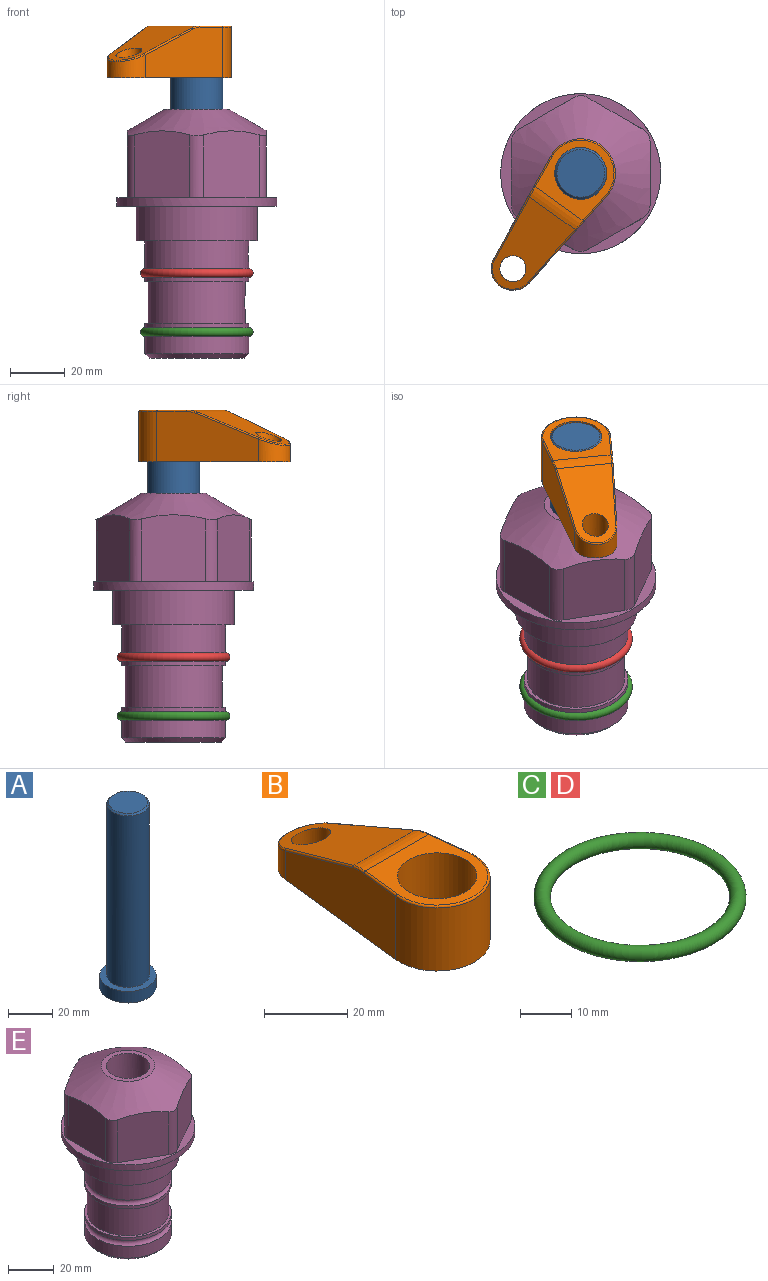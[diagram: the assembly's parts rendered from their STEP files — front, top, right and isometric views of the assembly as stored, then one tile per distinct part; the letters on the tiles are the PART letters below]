
ASSEMBLY  parts=5 mates=3
PART A: 6 faces, bbox 25.4x25.4x101.6 mm
  f0: plane 17.46x17.46mm, normal (0,0,1), area 239.5mm2, adj f5
  f1: plane 25.4x25.4mm, normal (0,0,-1), area 506.7mm2, adj f2
  f2: cylinder r=12.7mm len=25.4mm, axis (0,0,1), area 506.7mm2, adj f1,f3
  f3: plane 25.4x25.4mm, normal (0,0,1), area 221.7mm2, adj f2,f4
  f4: cylinder r=9.53mm len=94.46mm, axis (0,0,1), area 5653mm2, adj f3,f5
  f5: cone r=8.73mm half-angle=45deg, axis (0,0,-1), area 64.4mm2, adj f0,f4
PART B: 44 faces, bbox 27.5x64.5x19.1 mm
  f0: plane 2.3x0.95mm, normal (0,0,-1), area 1mm2, adj f25,f30,f34
  f1: plane 63.5x25.4mm, normal (0,0,-1), area 561.7mm2, adj f2,f3,f4,f5,f6,f7,f19,f20
  f2: cylinder r=12.7mm len=25.4mm, axis (0,0,-1), area 792.2mm2, adj f1,f3,f5,f13
  f3: plane 42.33x18.54mm, normal (0.99,0.11,0), area 647mm2, adj f1,f2,f4,f11,f12,f14
  f4: cylinder r=7.94mm len=15.78mm, axis (0,0,-1), area 158.6mm2, adj f1,f3,f5,f16
  f5: plane 42.33x18.54mm, normal (-0.99,0.11,0), area 647mm2, adj f1,f2,f4,f15,f17,f18
  f6: cylinder r=9.53mm len=19.05mm, axis (0,0,-1), area 1140.1mm2, adj f1,f8
  f7: cylinder r=4.76mm len=10.98mm, axis (0,0,-1), area 276.1mm2, adj f1,f9
  f8: plane 25.83x24.38mm, normal (0,0,1), area 262.2mm2, adj f6,f10,f11,f13,f15
  f9: plane 32.49x20.55mm, normal (0,0.34,0.94), area 489.9mm2, adj f7,f10,f14,f16,f18
  f10: cylinder r=12.7mm len=21.49mm, axis (-1,0,0), area 93.2mm2, adj f8,f9,f12,f17
  f11: cylinder r=0.51mm len=12.34mm, axis (0.11,-0.99,0), area 9.9mm2, adj f3,f8,f12,f13
  f12: bspline ~7.62x1.64mm, area 3.5mm2, adj f3,f10,f11,f14
  f13: torus R=12.19mm, axis (0,0,1), area 33.6mm2, adj f2,f8,f11,f15
  f14: cylinder r=0.51mm len=26.01mm, axis (0.1,-0.93,0.34), area 21.6mm2, adj f3,f9,f12,f16
  f15: cylinder r=0.51mm len=12.34mm, axis (0.11,0.99,0), area 9.9mm2, adj f5,f8,f13,f17
  f16: bspline ~15.78x7.05mm, area 15.7mm2, adj f4,f9,f14,f18
  f17: bspline ~7.62x1.64mm, area 3.5mm2, adj f5,f10,f15,f18
  f18: cylinder r=0.51mm len=26.01mm, axis (0.1,0.93,-0.34), area 21.6mm2, adj f5,f9,f16,f17
  f19: plane 21.6x14.29mm, normal (-0.99,-0.11,0), area 242.6mm2, adj f1,f26,f28,f34,f36,f38
  f20: plane 21.6x14.29mm, normal (0.99,-0.11,0), area 242.6mm2, adj f1,f27,f29,f37,f39,f41
  f21: cylinder r=12.7mm len=14.29mm, axis (0,0,-1), area 173.2mm2, adj f1,f26,f27,f30,f31,f33
  f22: cylinder r=7.94mm len=7.63mm, axis (0,0,-1), area 53.8mm2, adj f1,f28,f29,f42
  f23: plane 2.3x0.95mm, normal (0,0,-1), area 1mm2, adj f25,f33,f37
  f24: plane 17.94x12.32mm, normal (0,-0.34,-0.94), area 191.2mm2, adj f25,f38,f41,f42
  f25: cylinder r=9.53mm len=12.93mm, axis (-1,0,0), area 37.5mm2, adj f0,f23,f24,f31,f36,f39
  f26: cylinder r=1.59mm len=14.29mm, axis (0,0,-1), area 49mm2, adj f1,f19,f21,f32
  f27: cylinder r=1.59mm len=14.29mm, axis (0,0,-1), area 49mm2, adj f1,f20,f21,f35
  f28: cylinder r=1.59mm len=7.28mm, axis (0,0,-1), area 22.1mm2, adj f1,f19,f22,f40
  f29: cylinder r=1.59mm len=7.28mm, axis (0,0,-1), area 22.1mm2, adj f1,f20,f22,f43
  f30: torus R=14.29mm, axis (0,0,1), area 5.8mm2, adj f0,f21,f31,f32
  f31: bspline ~11.06x2.73mm, area 20.8mm2, adj f21,f25,f30,f33
  f32: sphere r=1.59mm, area 5.4mm2, adj f26,f30,f34
  f33: torus R=14.29mm, axis (0,0,1), area 5.8mm2, adj f21,f23,f31,f35
  f34: cylinder r=1.59mm len=1.68mm, axis (-0.11,0.99,0), area 2.4mm2, adj f0,f19,f32,f36
  f35: sphere r=1.59mm, area 5.4mm2, adj f27,f33,f37
  f36: bspline ~5.82x2.33mm, area 7.7mm2, adj f19,f25,f34,f38
  f37: cylinder r=1.59mm len=1.68mm, axis (0.11,0.99,0), area 2.4mm2, adj f20,f23,f35,f39
  f38: cylinder r=1.59mm len=18.33mm, axis (0.1,-0.93,0.34), area 46.7mm2, adj f19,f24,f36,f40
  f39: bspline ~5.82x2.33mm, area 7.7mm2, adj f20,f25,f37,f41
  f40: sphere r=1.59mm, area 3.6mm2, adj f28,f38,f42
  f41: cylinder r=1.59mm len=18.33mm, axis (0.1,0.93,-0.34), area 46.7mm2, adj f20,f24,f39,f43
  f42: bspline ~8.31x1.84mm, area 15.3mm2, adj f22,f24,f40,f43
  f43: sphere r=1.59mm, area 3.6mm2, adj f29,f41,f42
PART C: 1 faces, bbox 44.7x44.7x3.2 mm
  f0: torus R=19.05mm, axis (0,0,1), area 1193.9mm2
PART D: same geometry as C
PART E: 36 faces, bbox 58.7x58.7x91.2 mm
  f0: cylinder r=17.78mm len=35.56mm, axis (0,0,1), area 1670.8mm2, adj f23,f24,f31
  f1: cylinder r=19.05mm len=38.1mm, axis (0,0,1), area 1191.9mm2, adj f26,f27,f30
  f2: plane 58.66x58.66mm, normal (0,0,-1), area 1150.6mm2, adj f3,f28
  f3: cylinder r=29.33mm len=58.66mm, axis (0,0,-1), area 585.1mm2, adj f2,f4
  f4: plane 58.66x58.66mm, normal (0,0,1), area 475.9mm2, adj f3,f5,f6,f7,f8,f9,f10,f11
  f5: plane 24.5x20.32mm, normal (-0.5,0.87,0), area 562.8mm2, adj f4,f15,f16,f17
  f6: plane 24.5x20.32mm, normal (0.5,0.87,0), area 562.8mm2, adj f4,f14,f15,f17
  f7: plane 24.5x23.48mm, normal (1,0,0), area 562.8mm2, adj f4,f13,f14,f17
  f8: plane 24.5x20.32mm, normal (0.5,-0.87,0), area 562.8mm2, adj f4,f12,f13,f17
  f9: plane 24.5x20.32mm, normal (-0.5,-0.87,0), area 562.8mm2, adj f4,f11,f12,f17
  f10: plane 24.5x23.48mm, normal (-1,0,0), area 562.8mm2, adj f4,f11,f16,f17
  f11: cylinder r=5.08mm len=23.01mm, axis (0,0,-1), area 121.2mm2, adj f4,f9,f10,f17
  f12: cylinder r=5.08mm len=23.01mm, axis (0,0,-1), area 121.2mm2, adj f4,f8,f9,f17
  f13: cylinder r=5.08mm len=23.01mm, axis (0,0,-1), area 121.2mm2, adj f4,f7,f8,f17
  f14: cylinder r=5.08mm len=23.01mm, axis (0,0,-1), area 121.2mm2, adj f4,f6,f7,f17
  f15: cylinder r=5.08mm len=23.01mm, axis (0,0,-1), area 121.2mm2, adj f4,f5,f6,f17
  f16: cylinder r=5.08mm len=23.01mm, axis (0,0,-1), area 121.2mm2, adj f4,f5,f10,f17
  f17: cone r=11.73mm half-angle=60deg, axis (0,0,-1), area 2071.8mm2, adj f5,f6,f7,f8,f9,f10,f11,f12
  f18: plane 23.46x23.46mm, normal (0,0,1), area 147.4mm2, adj f17,f35
  f19: plane 34.93x34.93mm, normal (0,0,-1), area 958mm2, adj f29
  f20: cylinder r=19.05mm len=38.1mm, axis (0,0,1), area 760.1mm2, adj f21,f29
  f21: torus R=19.05mm, axis (0,0,1), area 565.3mm2, adj f20,f22
  f22: cylinder r=19.05mm len=38.1mm, axis (0,0,1), area 190mm2, adj f21,f23
  f23: plane 38.1x38.1mm, normal (0,0,1), area 146.9mm2, adj f0,f22
  f24: plane 38.1x38.1mm, normal (0,0,-1), area 146.9mm2, adj f0,f25
  f25: cylinder r=19.05mm len=38.1mm, axis (0,0,1), area 190mm2, adj f24,f26
  f26: torus R=19.05mm, axis (0,0,1), area 565.3mm2, adj f1,f25
  f27: plane 44.45x44.45mm, normal (0,0,-1), area 411.7mm2, adj f1,f28
  f28: cylinder r=22.23mm len=44.45mm, axis (0,0,1), area 1773.5mm2, adj f2,f27
  f29: cone r=19.05mm half-angle=45deg, axis (0,0,1), area 257.5mm2, adj f19,f20
  f30: cylinder r=3.17mm len=6.75mm, axis (-1,0,0), area 128mm2, adj f1,f33
  f31: cylinder r=3.17mm len=6.35mm, axis (-1,0,0), area 102.5mm2, adj f0,f33
  f32: plane 25.4x25.4mm, normal (0,0,1), area 506.7mm2, adj f33
  f33: cylinder r=12.7mm len=66.42mm, axis (0,0,-1), area 5236.2mm2, adj f30,f31,f32,f34
  f34: cone r=9.53mm half-angle=30deg, axis (0,0,-1), area 443.4mm2, adj f33,f35
  f35: cylinder r=9.53mm len=19.05mm, axis (0,0,-1), area 849mm2, adj f18,f34
PLACE A rot(axis=(0,0,-1),125.5deg) t=(0,0,-7.57)mm
PLACE B rot(axis=(0,0,1),144.5deg) t=(0,0,47.04)mm
PLACE C t=(0,0,-21.59)mm
PLACE D at identity
PLACE E at identity fixed
MATE fastened C.f0 <-> E.f0  axis (0,0,1) through (0,0,-46.1)mm
MATE cylindrical A.f2 <-> E.f0  axis (0,0,1) through (0,0,18.07)mm
MATE fastened B.f2 <-> A.f2  axis (0,0,1) through (0,0,66.09)mm
